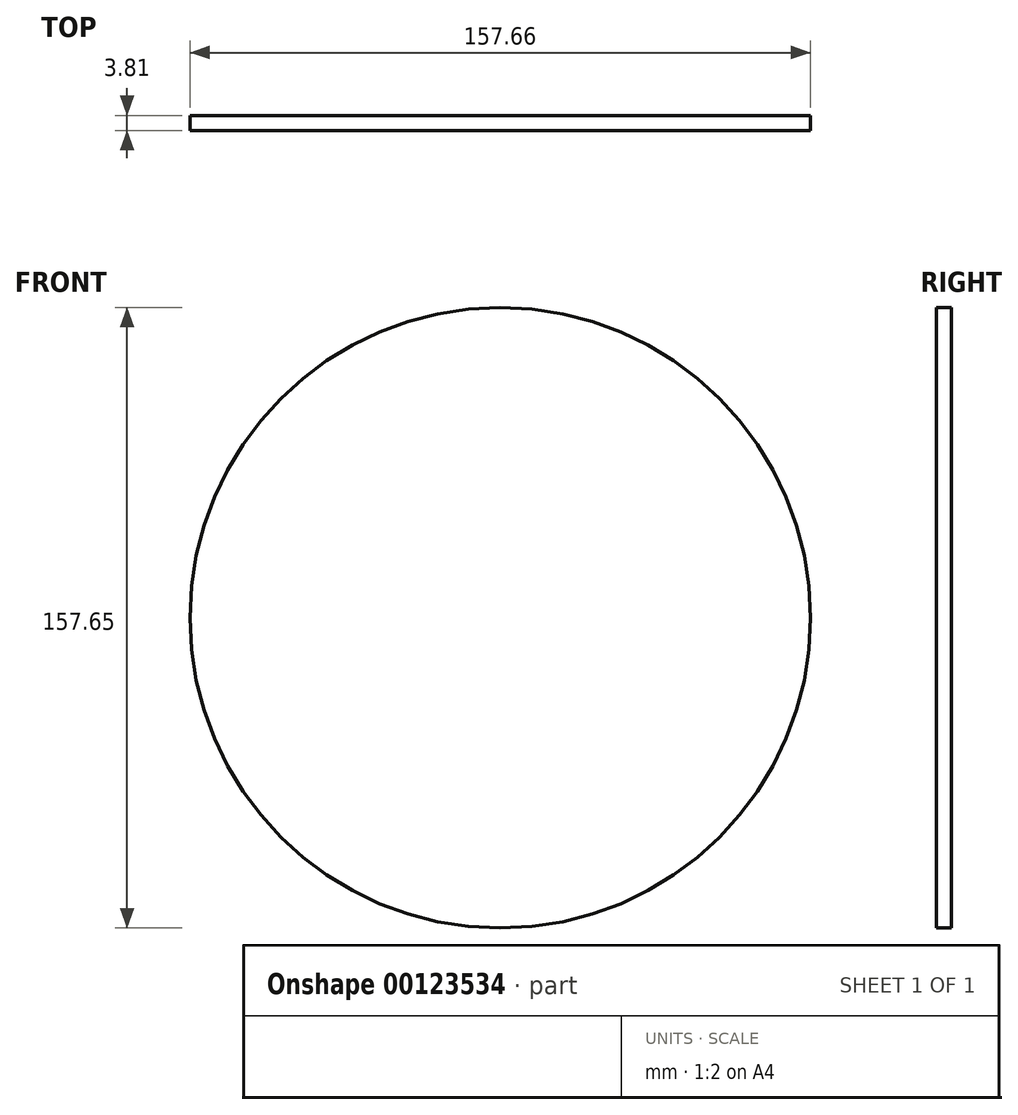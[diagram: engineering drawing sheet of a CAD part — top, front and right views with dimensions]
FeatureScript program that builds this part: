
annotation { "Feature Type Name" : "Feature", "Feature Type Description" : "" }
export const myFeature = defineFeature(function(context is Context, id is Id, definition is map)
    precondition{}
    {
        {
            var Q0;
            Q0=qCreatedBy(makeId("Front.planeOp"),FACE);
            var sketch = newSketch(context, id + "F0", { "sketchPlane" : qUnion([Q0])});
            skCircle(sketch, "E0", {"center": v(0, -2.63) * mm, "radius": 78.83 * mm});
            skSolve(sketch);
        }
        {
            var Q0;
            Q0=makeQuery(id+"F0.imprint","IMPRINT",FACE,{"disambiguationData":[TD([[makeQuery(id+"F0.imprint","IMPRINT",EDGE,{"derivedFrom":sQuery(id+"F0.wireOp",EDGE,"E0")}),1.0]])]});
            extrude(context, id + "F1", {"entities" : qUnion([Q0]), "depth" : 3.8 * mm});
        }
    });
